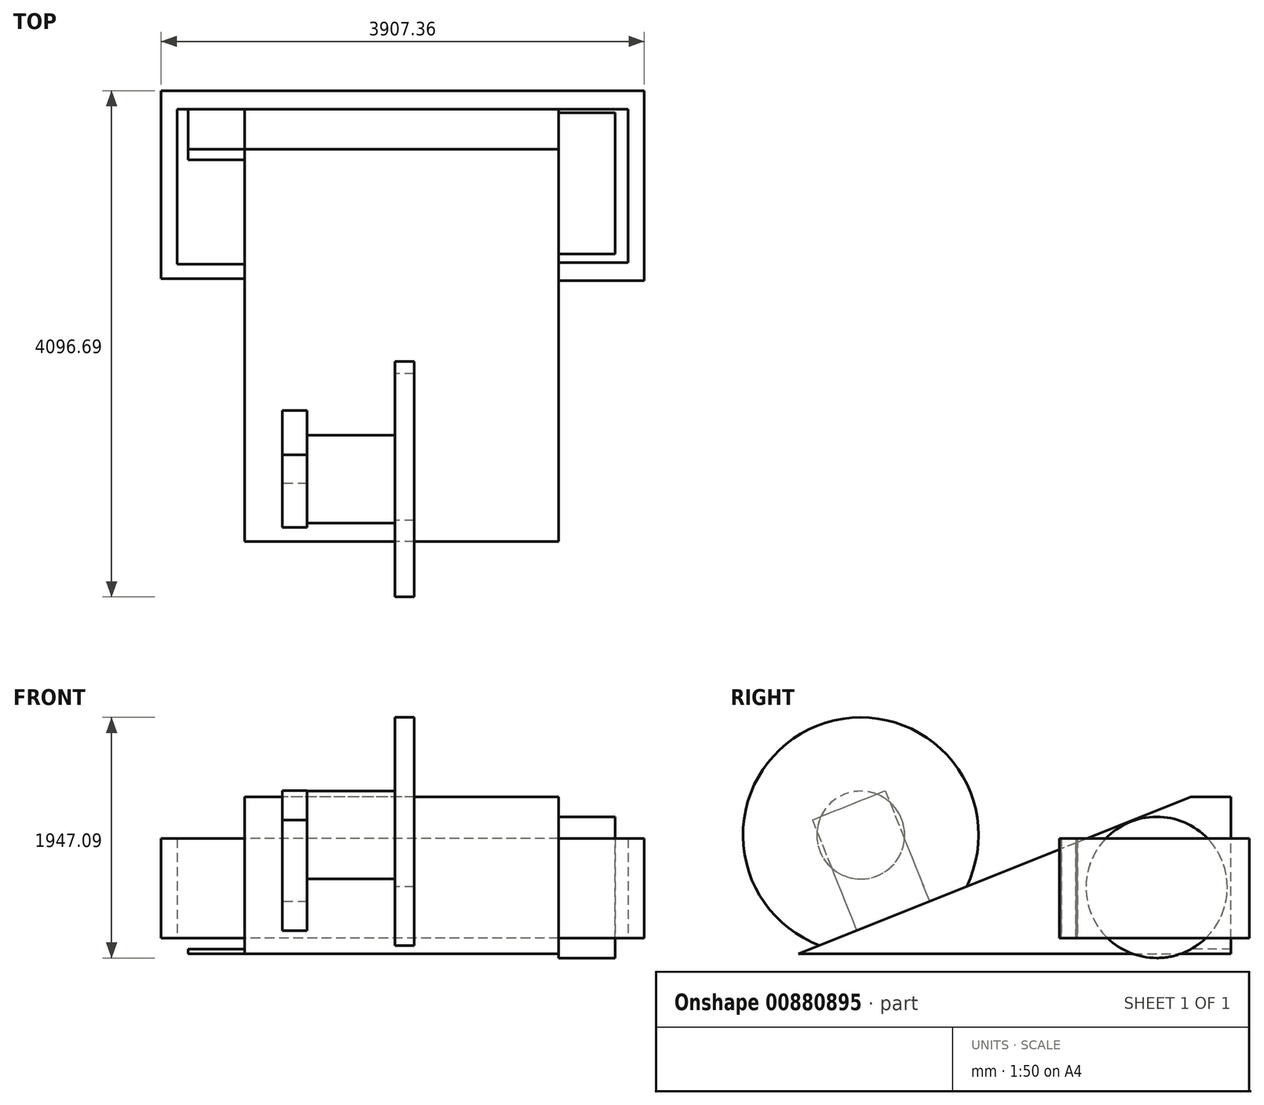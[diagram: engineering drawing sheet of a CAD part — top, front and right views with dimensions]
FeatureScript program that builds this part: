
annotation { "Feature Type Name" : "Feature", "Feature Type Description" : "" }
export const myFeature = defineFeature(function(context is Context, id is Id, definition is map)
    precondition{}
    {
        {
            var Q0;
            Q0=qCreatedBy(makeId("Right.planeOp"),FACE);
            var sketch = newSketch(context, id + "F0", { "sketchPlane" : qUnion([Q0])});
            skLineSegment(sketch, "E0", {"start": v(0, 0) * mm, "end": v(3175, 0) * mm});
            skLineSegment(sketch, "E1", {"start": v(3175, 0) * mm, "end": v(3175, 1270) * mm});
            skLineSegment(sketch, "E2", {"start": v(3175, 1270) * mm, "end": v(0, 0) * mm});
            skCircle(sketch, "E3", {"center": v(2898.32, 538.64) * mm, "radius": 571.5 * mm, "construction": true});
            skSolve(sketch);
        }
        {
            var Q0;
            Q0=makeQuery(id+"F0.imprint","IMPRINT",FACE,{"disambiguationData":[TD([[makeQuery(id+"F0.imprint","IMPRINT",EDGE,{"derivedFrom":sQuery(id+"F0.wireOp",EDGE,"E0")}),1.0]])]});
            extrude(context, id + "F1", {"entities" : qUnion([Q0]), "endBound" : BoundingType.SYMMETRIC, "depth" : 2540 * mm, "offsetDistance" : 25.4 * mm});
        }
        {
            var Q0;
            Q0=makeQuery(id+"F1.opExtrude","CAP_FACE",FACE,{"disambiguationData":[OSD([sQuery(id+"F0.wireOp",EDGE,"E0"),sQuery(id+"F0.wireOp",EDGE,"E1"),sQuery(id+"F0.wireOp",EDGE,"E2")])],"isStart":false});
            var sketch = newSketch(context, id + "F2", { "sketchPlane" : qUnion([Q0])});
            skCircle(sketch, "E4.0", {"center": v(2898.32, 538.64) * mm, "radius": 571.5 * mm});
            skSolve(sketch);
        }
        {
            var Q0;
            {var subQ0=sQuery(id+"F2.wireOp",EDGE,"E4.0");var subQ1=makeQuery(id+"F1.opExtrude","CAP_EDGE",EDGE,{"disambiguationData":[OSD([sQuery(id+"F0.wireOp",EDGE,"E1")])],"isStart":false});var subQ2=makeQuery(id+"F2.imprint","INTERSECT",VERTEX,{"disambiguationData":[OD(0.0)],"derivedFrom":[subQ1,subQ0]});Q0=makeQuery(id+"F2.imprint","IMPRINT",FACE,{"disambiguationData":[TD([[makeQuery(id+"F2.imprint","IMPRINT",EDGE,{"disambiguationData":[TD([[subQ2,1.0]])],"derivedFrom":subQ0}),1.0]])]});}
            var Q1;
            {var subQ0=sQuery(id+"F2.wireOp",EDGE,"E4.0");var subQ1=makeQuery(id+"F1.opExtrude","CAP_EDGE",EDGE,{"disambiguationData":[OSD([sQuery(id+"F0.wireOp",EDGE,"E1")])],"isStart":false});var subQ2=makeQuery(id+"F2.imprint","INTERSECT",VERTEX,{"disambiguationData":[OD(0.0)],"derivedFrom":[subQ1,subQ0]});Q1=makeQuery(id+"F2.imprint","IMPRINT",FACE,{"disambiguationData":[TD([[makeQuery(id+"F2.imprint","IMPRINT",EDGE,{"disambiguationData":[TD([[subQ2,-1.0]])],"derivedFrom":subQ0}),1.0]])]});}
            var Q2;
            {var subQ0=sQuery(id+"F2.wireOp",EDGE,"E4.0");var subQ1=makeQuery(id+"F1.opExtrude","CAP_EDGE",EDGE,{"disambiguationData":[OSD([sQuery(id+"F0.wireOp",EDGE,"E0")])],"isStart":false});var subQ2=makeQuery(id+"F2.imprint","INTERSECT",VERTEX,{"disambiguationData":[OD(0.0)],"derivedFrom":[subQ1,subQ0]});Q2=makeQuery(id+"F2.imprint","IMPRINT",FACE,{"disambiguationData":[TD([[makeQuery(id+"F2.imprint","IMPRINT",EDGE,{"disambiguationData":[TD([[subQ2,1.0]])],"derivedFrom":subQ0}),1.0]])]});}
            extrude(context, id + "F3", {"entities" : qUnion([Q0, Q1, Q2]), "operationType" : NewBodyOperationType.ADD, "depth" : 457.2 * mm, "offsetDistance" : 25.4 * mm});
        }
        {
            var Q0;
            Q0=makeQuery(id+"F1.opExtrude","CAP_FACE",FACE,{"disambiguationData":[OSD([sQuery(id+"F0.wireOp",EDGE,"E0"),sQuery(id+"F0.wireOp",EDGE,"E1"),sQuery(id+"F0.wireOp",EDGE,"E2")])],"isStart":true});
            var sketch = newSketch(context, id + "F4", { "sketchPlane" : qUnion([Q0])});
            skCircle(sketch, "E5.0", {"center": v(-2898.32, 538.64) * mm, "radius": 571.5 * mm});
            skSolve(sketch);
        }
        {
            var Q0;
            {var subQ0=sQuery(id+"F4.wireOp",EDGE,"E5.0");var subQ1=makeQuery(id+"F1.opExtrude","CAP_EDGE",EDGE,{"disambiguationData":[OSD([sQuery(id+"F0.wireOp",EDGE,"E1")])],"isStart":true});var subQ2=makeQuery(id+"F4.imprint","INTERSECT",VERTEX,{"disambiguationData":[OD(0.0)],"derivedFrom":[subQ1,subQ0]});Q0=makeQuery(id+"F4.imprint","IMPRINT",FACE,{"disambiguationData":[TD([[makeQuery(id+"F4.imprint","IMPRINT",EDGE,{"disambiguationData":[TD([[subQ2,-1.0]])],"derivedFrom":subQ0}),-1.0]])]});}
            var Q1;
            {var subQ0=sQuery(id+"F4.wireOp",EDGE,"E5.0");var subQ1=makeQuery(id+"F1.opExtrude","CAP_EDGE",EDGE,{"disambiguationData":[OSD([sQuery(id+"F0.wireOp",EDGE,"E0")])],"isStart":true});var subQ2=makeQuery(id+"F4.imprint","INTERSECT",VERTEX,{"disambiguationData":[OD(0.0)],"derivedFrom":[subQ1,subQ0]});Q1=makeQuery(id+"F4.imprint","IMPRINT",FACE,{"disambiguationData":[TD([[makeQuery(id+"F4.imprint","IMPRINT",EDGE,{"disambiguationData":[TD([[subQ2,-1.0]])],"derivedFrom":subQ0}),-1.0]])]});}
            var Q2;
            {var subQ0=sQuery(id+"F4.wireOp",EDGE,"E5.0");var subQ1=makeQuery(id+"F1.opExtrude","CAP_EDGE",EDGE,{"disambiguationData":[OSD([sQuery(id+"F0.wireOp",EDGE,"E0")])],"isStart":true});var subQ2=makeQuery(id+"F4.imprint","INTERSECT",VERTEX,{"disambiguationData":[OD(0.0)],"derivedFrom":[subQ1,subQ0]});Q2=makeQuery(id+"F4.imprint","IMPRINT",FACE,{"disambiguationData":[TD([[makeQuery(id+"F4.imprint","IMPRINT",EDGE,{"disambiguationData":[TD([[subQ2,1.0]])],"derivedFrom":subQ0}),-1.0]])]});}
            extrude(context, id + "F5", {"entities" : qUnion([Q0, Q1, Q2]), "operationType" : NewBodyOperationType.ADD, "depth" : 457.2 * mm, "offsetDistance" : 25.4 * mm});
        }
        {
            var Q0;
            {var subQ0=sQuery(id+"F0.wireOp",EDGE,"E2");var subQ1=sQuery(id+"F2.wireOp",EDGE,"E4.0");var subQ2=sQuery(id+"F0.wireOp",EDGE,"E1");var subQ3=sQuery(id+"F0.wireOp",EDGE,"E0");Q0=makeQuery(id+"F3.boolean.opBoolean","SPLIT",FACE,{"disambiguationData":[TD([makeQuery(id+"F1.opExtrude","SWEPT_FACE",FACE,{"disambiguationData":[OSD([subQ3])]}),makeQuery(id+"F1.opExtrude","SWEPT_FACE",FACE,{"disambiguationData":[OSD([subQ2])]}),makeQuery(id+"F1.opExtrude","SWEPT_FACE",FACE,{"disambiguationData":[OSD([subQ0])]}),makeQuery(id+"F3.opExtrude","SWEPT_FACE",FACE,{"disambiguationData":[OSD([subQ1])]}),makeQuery(id+"F3.opExtrude","CAP_FACE",FACE,{"disambiguationData":[OSD([subQ1])],"isStart":true})])],"derivedFrom":makeQuery(id+"F1.opExtrude","CAP_FACE",FACE,{"disambiguationData":[OSD([subQ3,subQ2,subQ0])],"isStart":false})});}
            var sketch = newSketch(context, id + "F6", { "sketchPlane" : qUnion([Q0])});
            skLineSegment(sketch, "E6.bottom", {"start": v(2256.67, 127) * mm, "end": v(2112.53, 127) * mm});
            skLineSegment(sketch, "E6.top", {"start": v(2256.67, 932.94) * mm, "end": v(2112.53, 932.94) * mm});
            skLineSegment(sketch, "E6.left", {"start": v(2256.67, 127) * mm, "end": v(2256.67, 932.94) * mm});
            skLineSegment(sketch, "E6.right", {"start": v(2112.53, 127) * mm, "end": v(2112.53, 932.94) * mm});
            skSolve(sketch);
        }
        {
            var Q0;
            {var subQ0=sQuery(id+"F6.wireOp",EDGE,"E6.bottom");Q0=makeQuery(id+"F6.imprint","IMPRINT",FACE,{"disambiguationData":[TD([[makeQuery(id+"F6.imprint","IMPRINT",EDGE,{"derivedFrom":subQ0}),-1.0]])]});}
            var Q1;
            {var subQ0=sQuery(id+"F6.wireOp",EDGE,"E6.top");Q1=makeQuery(id+"F6.imprint","IMPRINT",FACE,{"disambiguationData":[TD([[makeQuery(id+"F6.imprint","IMPRINT",EDGE,{"derivedFrom":subQ0}),1.0]])]});}
            extrude(context, id + "F7", {"entities" : qUnion([Q0, Q1]), "operationType" : NewBodyOperationType.ADD, "depth" : 693.42 * mm, "offsetDistance" : 25.4 * mm});
        }
        {
            var Q0;
            Q0=makeQuery(id+"F7.opExtrude","SWEPT_FACE",FACE,{"disambiguationData":[OSD([sQuery(id+"F6.wireOp",EDGE,"E6.left")])]});
            var sketch = newSketch(context, id + "F8", { "sketchPlane" : qUnion([Q0])});
            skLineSegment(sketch, "E7.bottom", {"start": v(-1963.42, 932.94) * mm, "end": v(-1833.04, 932.94) * mm});
            skLineSegment(sketch, "E7.top", {"start": v(-1963.42, 127) * mm, "end": v(-1833.04, 127) * mm});
            skLineSegment(sketch, "E7.left", {"start": v(-1963.42, 932.94) * mm, "end": v(-1963.42, 127) * mm});
            skLineSegment(sketch, "E7.right", {"start": v(-1833.04, 932.94) * mm, "end": v(-1833.04, 127) * mm});
            skSolve(sketch);
        }
        {
            var Q0;
            Q0=makeQuery(id+"F8.imprint","IMPRINT",FACE,{"disambiguationData":[TD([[makeQuery(id+"F8.imprint","IMPRINT",EDGE,{"derivedFrom":sQuery(id+"F8.wireOp",EDGE,"E7.bottom")}),-1.0]])]});
            extrude(context, id + "F9", {"entities" : qUnion([Q0]), "operationType" : NewBodyOperationType.ADD, "depth" : 1391.92 * mm, "offsetDistance" : 25.4 * mm});
        }
        {
            var Q0;
            Q0=makeQuery(id+"F9.opExtrude","SWEPT_FACE",FACE,{"disambiguationData":[OSD([sQuery(id+"F8.wireOp",EDGE,"E7.right")])]});
            var sketch = newSketch(context, id + "F10", { "sketchPlane" : qUnion([Q0])});
            skLineSegment(sketch, "E8.bottom", {"start": v(-3648.59, 932.94) * mm, "end": v(-3499.62, 932.94) * mm});
            skLineSegment(sketch, "E8.top", {"start": v(-3648.59, 127) * mm, "end": v(-3499.62, 127) * mm});
            skLineSegment(sketch, "E8.left", {"start": v(-3648.59, 932.94) * mm, "end": v(-3648.59, 127) * mm});
            skLineSegment(sketch, "E8.right", {"start": v(-3499.62, 932.94) * mm, "end": v(-3499.62, 127) * mm});
            skSolve(sketch);
        }
        {
            var Q0;
            Q0=makeQuery(id+"F10.imprint","IMPRINT",FACE,{"disambiguationData":[TD([[makeQuery(id+"F10.imprint","IMPRINT",EDGE,{"derivedFrom":sQuery(id+"F10.wireOp",EDGE,"E8.bottom")}),-1.0]])]});
            extrude(context, id + "F11", {"entities" : qUnion([Q0]), "operationType" : NewBodyOperationType.ADD, "depth" : 3776.98 * mm, "offsetDistance" : 25.4 * mm});
        }
        {
            var Q0;
            Q0=makeQuery(id+"F11.opExtrude","SWEPT_FACE",FACE,{"disambiguationData":[OSD([sQuery(id+"F10.wireOp",EDGE,"E8.right")])]});
            var sketch = newSketch(context, id + "F12", { "sketchPlane" : qUnion([Q0])});
            skLineSegment(sketch, "E9.bottom", {"start": v(-1943.94, 932.94) * mm, "end": v(-1813.35, 932.94) * mm});
            skLineSegment(sketch, "E9.top", {"start": v(-1943.94, 127) * mm, "end": v(-1813.35, 127) * mm});
            skLineSegment(sketch, "E9.left", {"start": v(-1943.94, 932.94) * mm, "end": v(-1943.94, 127) * mm});
            skLineSegment(sketch, "E9.right", {"start": v(-1813.35, 932.94) * mm, "end": v(-1813.35, 127) * mm});
            skSolve(sketch);
        }
        {
            var Q0;
            Q0=makeQuery(id+"F12.imprint","IMPRINT",FACE,{"disambiguationData":[TD([[makeQuery(id+"F12.imprint","IMPRINT",EDGE,{"derivedFrom":sQuery(id+"F12.wireOp",EDGE,"E9.bottom")}),-1.0]])]});
            extrude(context, id + "F13", {"entities" : qUnion([Q0]), "operationType" : NewBodyOperationType.ADD, "depth" : 1371.6 * mm, "offsetDistance" : 25.4 * mm});
        }
        {
            var Q0;
            Q0=makeQuery(id+"F13.opExtrude","SWEPT_FACE",FACE,{"disambiguationData":[OSD([sQuery(id+"F12.wireOp",EDGE,"E9.right")])]});
            var sketch = newSketch(context, id + "F14", { "sketchPlane" : qUnion([Q0])});
            skLineSegment(sketch, "E10.bottom", {"start": v(2128.02, 932.94) * mm, "end": v(2245.68, 932.94) * mm});
            skLineSegment(sketch, "E10.top", {"start": v(2128.02, 127) * mm, "end": v(2245.68, 127) * mm});
            skLineSegment(sketch, "E10.left", {"start": v(2128.02, 932.94) * mm, "end": v(2128.02, 127) * mm});
            skLineSegment(sketch, "E10.right", {"start": v(2245.68, 932.94) * mm, "end": v(2245.68, 127) * mm});
            skSolve(sketch);
        }
        {
            var Q0;
            Q0=makeQuery(id+"F14.imprint","IMPRINT",FACE,{"disambiguationData":[TD([[makeQuery(id+"F14.imprint","IMPRINT",EDGE,{"derivedFrom":sQuery(id+"F14.wireOp",EDGE,"E10.bottom")}),-1.0]])]});
            extrude(context, id + "F15", {"entities" : qUnion([Q0]), "operationType" : NewBodyOperationType.ADD, "depth" : 543.56 * mm, "offsetDistance" : 25.4 * mm});
        }
        {
            var Q0;
            Q0=makeQuery(id+"F1.opExtrude","SWEPT_FACE",FACE,{"disambiguationData":[OSD([sQuery(id+"F0.wireOp",EDGE,"E2")])]});
            var sketch = newSketch(context, id + "F16", { "sketchPlane" : qUnion([Q0])});
            skLineSegment(sketch, "E11.bottom", {"start": v(-762, 508) * mm, "end": v(-965.2, 508) * mm});
            skLineSegment(sketch, "E11.top", {"start": v(-762, 1143) * mm, "end": v(-965.2, 1143) * mm});
            skLineSegment(sketch, "E11.left", {"start": v(-762, 508) * mm, "end": v(-762, 1143) * mm});
            skLineSegment(sketch, "E11.right", {"start": v(-965.2, 508) * mm, "end": v(-965.2, 1143) * mm});
            skSolve(sketch);
        }
        {
            var Q0;
            Q0=makeQuery(id+"F16.imprint","IMPRINT",FACE,{"disambiguationData":[TD([[makeQuery(id+"F16.imprint","IMPRINT",EDGE,{"derivedFrom":sQuery(id+"F16.wireOp",EDGE,"E11.bottom")}),-1.0]])]});
            extrude(context, id + "F17", {"entities" : qUnion([Q0]), "operationType" : NewBodyOperationType.ADD, "depth" : 965.2 * mm, "offsetDistance" : 25.4 * mm});
        }
        {
            var Q0;
            Q0=makeQuery(id+"F17.opExtrude","SWEPT_FACE",FACE,{"disambiguationData":[OSD([sQuery(id+"F16.wireOp",EDGE,"E11.left")])]});
            var sketch = newSketch(context, id + "F18", { "sketchPlane" : qUnion([Q0])});
            skCircle(sketch, "E12", {"center": v(504.4, 961.73) * mm, "radius": 355.6 * mm});
            skSolve(sketch);
        }
        {
            var Q0;
            {var subQ0=sQuery(id+"F18.wireOp",EDGE,"E12");var subQ1=makeQuery(id+"F17.opExtrude","CAP_EDGE",EDGE,{"disambiguationData":[OSD([sQuery(id+"F16.wireOp",EDGE,"E11.left")])],"isStart":false});var subQ2=makeQuery(id+"F18.imprint","INTERSECT",VERTEX,{"disambiguationData":[OD(0.0)],"derivedFrom":[subQ1,subQ0]});Q0=makeQuery(id+"F18.imprint","IMPRINT",FACE,{"disambiguationData":[TD([[makeQuery(id+"F18.imprint","IMPRINT",EDGE,{"disambiguationData":[TD([[subQ2,-1.0]])],"derivedFrom":subQ0}),1.0]])]});}
            var Q1;
            {var subQ0=sQuery(id+"F18.wireOp",EDGE,"E12");var subQ1=makeQuery(id+"F17.opExtrude","SWEPT_EDGE",EDGE,{"disambiguationData":[OSD([sQuery(id+"F16.wireOp",EDGE,"E11.top"),sQuery(id+"F16.wireOp",EDGE,"E11.left")])]});var subQ2=makeQuery(id+"F18.imprint","INTERSECT",VERTEX,{"disambiguationData":[OD(0.0)],"derivedFrom":[subQ1,subQ0]});Q1=makeQuery(id+"F18.imprint","IMPRINT",FACE,{"disambiguationData":[TD([[makeQuery(id+"F18.imprint","IMPRINT",EDGE,{"disambiguationData":[TD([[subQ2,1.0]])],"derivedFrom":subQ0}),1.0]])]});}
            var Q2;
            {var subQ0=sQuery(id+"F18.wireOp",EDGE,"E12");var subQ1=sQuery(id+"F16.wireOp",EDGE,"E11.left");var subQ7=makeQuery(id+"F17.opExtrude","CAP_EDGE",EDGE,{"disambiguationData":[OSD([subQ1])],"isStart":false});var subQ8=makeQuery(id+"F18.imprint","INTERSECT",VERTEX,{"disambiguationData":[OD(0.0)],"derivedFrom":[subQ7,subQ0]});Q2=makeQuery(id+"F18.imprint","IMPRINT",FACE,{"disambiguationData":[TD([[makeQuery(id+"F18.imprint","IMPRINT",EDGE,{"disambiguationData":[TD([[subQ8,1.0]])],"derivedFrom":subQ7}),-1.0]])]});}
            var Q3;
            {var subQ0=sQuery(id+"F18.wireOp",EDGE,"E12");var subQ1=makeQuery(id+"F17.opExtrude","SWEPT_EDGE",EDGE,{"disambiguationData":[OSD([sQuery(id+"F16.wireOp",EDGE,"E11.bottom"),sQuery(id+"F16.wireOp",EDGE,"E11.left")])]});var subQ2=makeQuery(id+"F18.imprint","INTERSECT",VERTEX,{"disambiguationData":[OD(0.0)],"derivedFrom":[subQ1,subQ0]});Q3=makeQuery(id+"F18.imprint","IMPRINT",FACE,{"disambiguationData":[TD([[makeQuery(id+"F18.imprint","IMPRINT",EDGE,{"disambiguationData":[TD([[subQ2,-1.0]])],"derivedFrom":subQ0}),1.0]])]});}
            extrude(context, id + "F19", {"entities" : qUnion([Q0, Q1, Q2, Q3]), "operationType" : NewBodyOperationType.ADD, "depth" : 711.2 * mm, "offsetDistance" : 25.4 * mm});
        }
        {
            var Q0;
            Q0=makeQuery(id+"F19.opExtrude","CAP_FACE",FACE,{"disambiguationData":[OSD([sQuery(id+"F18.wireOp",EDGE,"E12")])],"isStart":false});
            var sketch = newSketch(context, id + "F20", { "sketchPlane" : qUnion([Q0])});
            skCircle(sketch, "E13", {"center": v(504.4, 961.73) * mm, "radius": 952.5 * mm});
            skSolve(sketch);
        }
        {
            var Q0;
            Q0 = qSketchRegion(id + "F20", true);
            extrude(context, id + "F21", {"entities" : qUnion([Q0]), "operationType" : NewBodyOperationType.ADD, "depth" : 152.4 * mm, "offsetDistance" : 25.4 * mm});
        }
        {
            var Q0;
            Q0=makeQuery(id+"F1.opExtrude","SWEPT_FACE",FACE,{"disambiguationData":[OSD([sQuery(id+"F0.wireOp",EDGE,"E1")])]});
            extrude(context, id + "F22", {"entities" : qUnion([Q0]), "operationType" : NewBodyOperationType.ADD, "depth" : 325.12 * mm, "offsetDistance" : 25.4 * mm});
        }
    });
